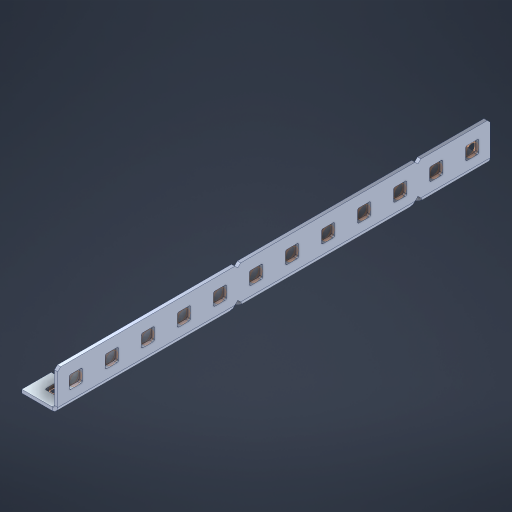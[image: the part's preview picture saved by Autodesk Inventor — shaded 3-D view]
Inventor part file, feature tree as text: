
AUTODESK INVENTOR PART (.ipt)
format: ipt  version: 2023 (Build 270158000, 158)  size: 730,112 bytes
history: native  units: in
note: dims shown in document units (in); Inventor stores cm internally (conversion verified against a paired STEP export)
features: other x43, extrude x34, sheet_metal_op x11, sketch x10, pattern_linear x2, mirror x1, chamfer x1
ambient origin geometry x8: Origin, YZ Plane, XZ Plane, XY Plane, X Axis, Y Axis, Z Axis, Center Point
bodies: Solid1 (feature_tree), Body (feature_tree)
feature tree (102):
  sheet_metal_op  "Flanges"
  other  "Flange Pattern Plane"
  other  "Flange Pattern Sketch"
  sheet_metal_op  "Flange Pattern"
  sheet_metal_op  "Body Pattern"
  pattern_linear  "Center Pattern"  Spacing1=0.0469in  [1 undecoded]
  other  "Arc Length"
  mirror  "Notch Mirror"
  pattern_linear  "Notch Pattern"  Spacing1=0.182in  [1 undecoded]
  chamfer  "End Chamfer"
  extrude  "Half Cut"  Depth=0.02in
  sketch  "Sketch1"  dims[d0=1.0in]
  other  "Plate1"
  sketch  "Sketch2"  dims[d1=6.0in]
  other  "Plate2"
  sheet_metal_op  "Bend1"
  sheet_metal_op  "Corner1"
  sketch  "Sketch3"  dims[d2=0.0469in]
  sketch  "Sketch7"  dims[d3=0.0469in]
  other  "Srf1"
  other  "Srf2"
  sketch  "Sketch8"  dims[d4=0.0234in]
  sketch  "Sketch9"  dims[d5=0.0938in]
  other  "Srf91"
  sheet_metal_op  "Body Pattern Sketch"
  other  "Srf92"
  sketch  "Sketch13"  dims[d6=0.0469in]
  sketch  "Sketch14"  dims[d7=0.5in d8=90.0deg d9=0.0312in]
  sketch  "Sketch15"  dims[d10=0.1875in]
  sketch  "Sketch16"  dims[d11=0.0469in d12=0.0469in d16=0.182in d17=0.02in d18=0.0469in d19=0.0in d20=0.25in d21=0.25in d38=4.7244in d40=0.5in d41=0.3937in d43=1.0in d46=0.172in d47=1.0in d48=0.0in d49=0.182in d50=0.02in d51=0.25in d52=0.25in d53=0.0469in d54=0.0in d55=0.172in d56=1.0in d57=0.0in d58=0.25in d60=4.7244in d62=0.5in d63=0.3937in d65=0.5in d85=0.1227in d86=0.1659in d88=0.04in d89=0.0469in d90=0.0in d91=0.04in d92=0.0491in d95=2.5in d96=0.04in d97=0.25in d98=45.0deg d99=0.25in d100=0.5in d101=0.0in d102=2.497in d106=0.182in d107=0.02in d108=0.5in d109=0.5in d110=0.0469in d111=0.0in d112=0.172in d113=0.5in d114=0.0in d117=0.5in d118=0.5in d119=0.5in]
  other  "Srf786"
  other  "Srf823"
  other  "Srf824"
  other  "Srf825"
  other  "Srf826"
  other  "Srf827"
  other  "Srf828"
  other  "Srf829"
  other  "Srf856"
  other  "Srf857"
  other  "Srf858"
  other  "Srf859"
  other  "Srf860"
  other  "Srf861"
  other  "Srf862"
  other  "Srf889"
  other  "Srf890"
  other  "Srf891"
  other  "Srf892"
  other  "Srf893"
  other  "Srf894"
  other  "Srf895"
  other  "Srf896"
  other  "Srf922"
  other  "Srf923"
  other  "Srf924"
  other  "Srf959"
  other  "Srf960"
  other  "Srf961"
  other  "Srf996"
  other  "Srf997"
  other  "Srf998"
  sheet_metal_op  "Flange Stamp"
  sheet_metal_op  "Flange Circle"
  sheet_metal_op  "Body Stamp"
  sheet_metal_op  "Body Circle"
  other  "Center Stamp"
  other  "Center Circle"
  sheet_metal_op  "Notch"
  extrude  "ExtrusionSrf2"  Depth=0.0469in
  extrude  "ExtrusionSrf92"  TaperAngle=0.0deg  [1 undecoded]
  extrude  "ExtrusionSrf823"  Depth=0.25in
  extrude  "ExtrusionSrf824"  Depth=0.25in
  extrude  "ExtrusionSrf825"  Depth=0.5in
  extrude  "ExtrusionSrf826"  Depth=0.5in
  extrude  "ExtrusionSrf827"  Depth=1.0in TaperAngle=0.0deg
  extrude  "ExtrusionSrf828"  Depth=0.182in
  extrude  "ExtrusionSrf829"  Depth=0.02in
  extrude  "ExtrusionSrf856"  Depth=0.25in
  extrude  "ExtrusionSrf857"  Depth=0.25in
  extrude  "ExtrusionSrf858"  Depth=0.0469in
  extrude  "ExtrusionSrf859"  TaperAngle=0.0deg  [1 undecoded]
  extrude  "ExtrusionSrf860"  Depth=0.5in
  extrude  "ExtrusionSrf861"  Depth=1.0in TaperAngle=0.0deg
  extrude  "ExtrusionSrf862"  Depth=0.25in
  extrude  "ExtrusionSrf889"  Depth=0.5in
  extrude  "ExtrusionSrf890"  Depth=0.5in
  extrude  "ExtrusionSrf891"  Depth=0.5in
  extrude  "ExtrusionSrf892"  Depth=0.5in
  extrude  "ExtrusionSrf893"  Depth=0.5in
  extrude  "ExtrusionSrf894"  Depth=0.0469in
  extrude  "ExtrusionSrf895"  TaperAngle=0.0deg  [1 undecoded]
  extrude  "ExtrusionSrf896"  Depth=0.5in
  extrude  "ExtrusionSrf922"  Depth=0.5in
  extrude  "ExtrusionSrf923"  Depth=2.5in
  extrude  "ExtrusionSrf924"  Depth=0.25in TaperAngle=45.0deg
  extrude  "ExtrusionSrf959"  Depth=0.25in
  extrude  "ExtrusionSrf960"  Depth=0.5in TaperAngle=0.0deg
  extrude  "ExtrusionSrf961"  Depth=0.5in
  extrude  "ExtrusionSrf996"  Depth=0.182in
  extrude  "ExtrusionSrf997"  Depth=0.02in
  extrude  "ExtrusionSrf998"  Depth=0.5in
note: 5 required parameter values undecoded (feature->parameter linkage not recoverable at this tier; creation-order binding heuristic only, values carry confidence <= 0.55)
